# Revit family: 65252213
name_source: partatom
category: Plumbing Fixtures
units: mm (PartAtom-declared; Revit-internal decimal feet)

## family parameters
Always vertical = Yes
Cut with Voids When Loaded = No
OmniClass Number = 23.45.55.00
OmniClass Title = Sanitary Faucets, Wastes
Part Type = Normal
Room Calculation Point = No
Round Connector Dimension = Use Diameter
Shared = No
Work Plane-Based = No

## types (1)
- 65252213 Kitchen faucet, 230/5 V
    2D/3D/BIM Files URL = http://static.hansa.com
    3D View = https://static.hansa.com
    Additional Features = Soft- and Needle-Spray
    Advanced Features = Surfaces in contact with drinking water contain less than 0.3% lead;Waterways without nickel coating;Software settings adjustable via buttons
    Afterflow Period = 4 s (2/4/8/10/20 s)
    Ambience photo = http://static.hansa.com
    AssetType = Fixed
    Automatic Flush Frequency = off (off/12/24/48/72 h)
    Automatic Flush Period = 30 s (10/30/60/120/180 s)
    BIMObjectName = 65252213
    Backflow Prevention EN1717 = EB
    BodyMaterial = Brass
    Brand = HANSA
    Catalog Drawing URL = http://static.hansa.com
    Category = Kitchen
    CloseOffRating = 0
    Color = Chrome
    Connection = Flexible inlet pipes
    Connection Size = G3/8
    Default Elevation = 0 mm  [stored 0 ft]
    Dimension Drawing URL = http://static.hansa.com
    Diverter = Push operated diverter;Automatic reset
    DurationUnit = Year
    EAN Number = 4057304004513
    EMC Directive = Low Voltage Directive 2014/35/EU , 
EMC Directive 2014/30/EU , 
RoHS Directive 2011/65/EU
    EN Standard = EN 1111, EN 200 ,  EN 15091, ETSI EN 301 489-1 V1.9.2 , 
ETSI EN 300 328 v2.2.2 , 
EN 61000-6-1:2007 , 
EN 61000-6-3:2007+A1:2011+AC:2012 , 
EN 60335-1:2012+A11+A13+A1+A14+A2+A15:2021, Part 19.11.4
    ETIM Class Number = EC011431 Kitchen mixing tap
    Electrical Connection = 230 / 5 V
    Electronic Parts = Autofocus infrared sensor;Solenoid valve;Power supply;Light indicated function(s)
    FDV Document URL = http://www.hansa.com
    FaucetMainMaterial = Brass
    Features = Hybrid;Plug transformer
    Finish = Polished
    Flow Drawing URL = http://static.hansa.com
    Flow Rate At 300kPa = 0.2 L/s
    FlowCoefficient = 0
    Group = Kitchen faucet
    Hand Shower = Pull-out hand spray
    IfcExportAs = IfcValveType
    IfcExportType = FAUCET
    InletConnectionSize = 10 mm  [stored 0.0328084 ft]
    Installation Type = Deck mounted
    Installation and Maintenance Guide URL = http://static.hansa.com
    Interactive AR View URL = https://static.hansa.com
    Lever Handle = Easy-Grip surface;Two operating levers/handles
    Manufacturer = HANSA
    ManufacturerName = HANSA
    ManufacturerURL = http://www.hansa.com
    Market = International;Germany;Austria;Belgium;Netherlands;France;Czech Republic;Slovakia;Italy;Spain
    Material = Brass/Plastic
    Max Flow Period = 40 s (10/40/60/120/180 s)
    Max. Hot Water Supply = 70 °C
    Mechanical Parts = Ceramic head part for flow control;Mixing valve for manual temperature control;Litter filter(s)
    Mobile Product Information URL = http://mpi.hansa.com
    Model = 65252213 Kitchen faucet, 230/5 V
    ModelReference = 65252213
    Mounting Holes = 1 hole
    NBSDescription = Water supply fittings for wash basins and troughs
    NBSReference = 45-35-70/371
    Name = 65252213 Kitchen faucet, 230/5 V
    Name_en = 65252213 Kitchen faucet, 230/5 V
    NominalDepth = 249 mm
    NominalHeight = 482 mm
    NominalWidth = 122 mm
    Operating Distance = 0-40 mm
    Operating Voltage = 5 V
    Product Code = 65252213
    Product Family = HANSAFIT Semiprofessional
    Product Image URL = http://static.hansa.com
    Product URL = http://static.hansa.com
    Protection Class = IP 55 / transformer IP 20
    Sales Package dimensions (LxWxH) = 1017 x 230 x 144
    Shape = Sculptured
    Shower Spray = Normal;Intense
    Shower Spray Number = 2 shower sprays
    Size = 120x250x480 mm
    Spare-Part Information URL = http://static.hansa.com
    Spout Projection = 200 mm
    Spout Swivel Range = 120° (80° / 60°)
    Spout Type = Swivel spout
    Surface treatment = Chrome
    Technical DataSheet URL = http://www.hansa.com
    UNSPSC Class Number = 30181700 Faucets or taps
    URL Declaration Of Performance (DOP) = http://static.hansa.com
    URL Declaration of Asbestos = http://static.hansa.com
    URL Declaration of Conformity = http://static.hansa.com
    URL Declaration of SCIP = http://static.hansa.com
    URL EU Packaging Declaration = http://static.hansa.com
    URL EcoLabel Declaration = http://static.hansa.com
    URL REACH = http://static.hansa.com
    URL WEEE = http://static.hansa.com
    Uniclass2 = Pr_40_30_96_96
    Uniclass2015Description = Washbasin manual water supply sets
    Uniclass2015Reference = Pr_40_20_87_96
    Version = 1
    VersionDate = 01/06/2023
    Warranty Information URL = http://warranty.hansa.com
    WarrantyDescription = http://warranty.hansa.com
    WarrantyDurationUnit = Year
    Working Pressure = 100 - 1000 kPa

note: [stored X ft] marks values corroborated as IEEE doubles in the binary element streams (Revit-internal decimal feet)

## geometry (parser evidence)
native form markers: Sweep x6
no freeform markers — native parametric forms only
